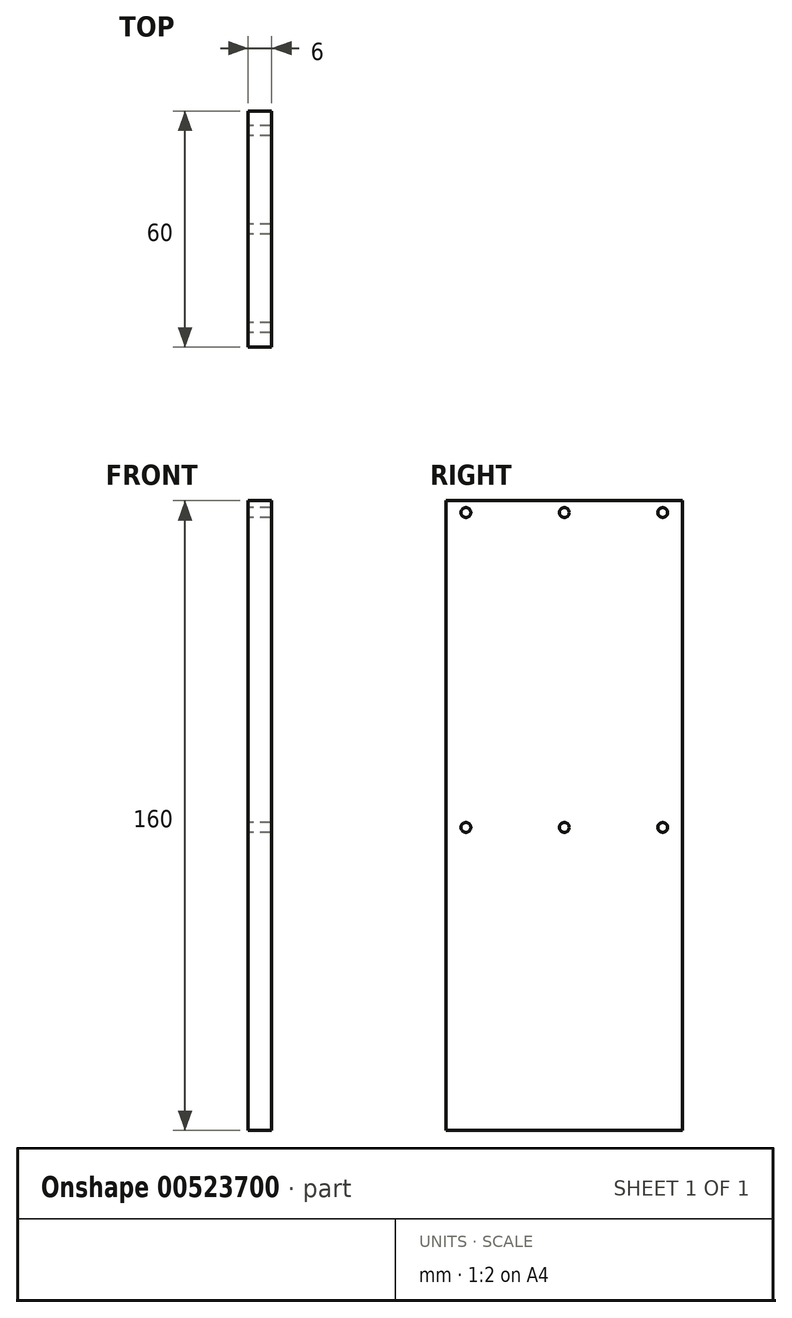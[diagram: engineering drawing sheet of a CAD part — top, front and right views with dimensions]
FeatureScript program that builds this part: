
annotation { "Feature Type Name" : "Feature", "Feature Type Description" : "" }
export const myFeature = defineFeature(function(context is Context, id is Id, definition is map)
    precondition{}
    {
        {
            var Q0;
            Q0=qCreatedBy(makeId("Right.planeOp"),FACE);
            var sketch = newSketch(context, id + "F0", { "sketchPlane" : qUnion([Q0])});
            skLineSegment(sketch, "E0.bottom", {"start": v(0, 0) * mm, "end": v(60, 0) * mm});
            skLineSegment(sketch, "E0.top", {"start": v(0, 160) * mm, "end": v(60, 160) * mm});
            skLineSegment(sketch, "E0.left", {"start": v(0, 0) * mm, "end": v(0, 160) * mm});
            skLineSegment(sketch, "E0.right", {"start": v(60, 0) * mm, "end": v(60, 160) * mm});
            skCircle(sketch, "E1", {"center": v(5, 77) * mm, "radius": 1.25 * mm});
            skCircle(sketch, "E2", {"center": v(30, 77) * mm, "radius": 1.25 * mm});
            skCircle(sketch, "E3", {"center": v(55, 77) * mm, "radius": 1.25 * mm});
            skCircle(sketch, "E4", {"center": v(5, 157) * mm, "radius": 1.25 * mm});
            skCircle(sketch, "E5", {"center": v(30, 157) * mm, "radius": 1.25 * mm});
            skCircle(sketch, "E6", {"center": v(55, 157) * mm, "radius": 1.25 * mm});
            skSolve(sketch);
        }
        {
            var Q0;
            Q0=makeQuery(id+"F0.imprint","IMPRINT",FACE,{"disambiguationData":[TD([[makeQuery(id+"F0.imprint","IMPRINT",EDGE,{"derivedFrom":sQuery(id+"F0.wireOp",EDGE,"E0.bottom")}),1.0]])]});
            extrude(context, id + "F1", {"entities" : qUnion([Q0]), "depth" : 6 * mm, "offsetDistance" : 25 * mm});
        }
    });
